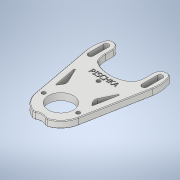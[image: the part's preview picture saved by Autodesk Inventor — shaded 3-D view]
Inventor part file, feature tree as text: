
AUTODESK INVENTOR PART (.ipt)
format: ipt  version: 2020.1 (Build 241239000, 239)  size: 804,864 bytes
history: native  units: mm
features: thread x3, sketch x3, emboss x2, fillet x2, extrude x1, chamfer x1, other x1
ambient origin geometry x8: Origin, YZ Plane, XZ Plane, XY Plane, X Axis, Y Axis, Z Axis, Center Point
bodies: Body1 (feature_tree)
feature tree (13):
  extrude  "Extrusion3"  Depth=20.0mm
  thread  "Thread1"  [1 undecoded]
  thread  "Thread2"  [1 undecoded]
  thread  "Thread3"  [1 undecoded]
  emboss  "Emboss1"
  emboss  "Emboss2"
  fillet  "Fillet3"  Radius=3.5mm
  fillet  "Fillet5"  Radius=32.0mm
  chamfer  "Chamfer3"  Distance=3.0mm
  other  "Center Lines"
  sketch  "Sketch1"  dims[d0=51.5mm d1=20.0mm d3=3.5mm d4=3.5mm d5=7.0mm d9=3.5mm d11=32.0mm]
  sketch  "Sketch3"  dims[d15=4.1mm]
  sketch  "Sketch4"  dims[d24=3.0mm d25=3.0mm d27=45.0deg d29=3.0mm d30=3.0mm d40=5.5mm d41=0.0mm d44=10.0mm d45=0.0mm d46=10.0mm d47=0.0mm d48=10.0mm d49=0.0mm d50=10.0mm d51=52.0mm d53=27.0mm d65=0.2mm d66=0.0mm d67=2.0mm d68=2.0mm d69=5.0mm d70=25.0mm d71=5.0mm d72=25.0mm d73=0.2mm d74=0.0mm d75=80.75mm d76=7.5mm d77=3.75mm d81=6.25mm d82=12.5mm d85=5.0mm d86=4.0mm d91=0.5mm d94=2.0mm d95=0.5mm d96=2.0mm d97=45.0deg d98=15.0deg d99=24.0mm d102=43.0mm d103=2.0mm d109=7.0mm d110=7.0mm d113=3.332mm d115=42.484mm]
note: 3 required parameter values undecoded (feature->parameter linkage not recoverable at this tier; creation-order binding heuristic only, values carry confidence <= 0.55)
